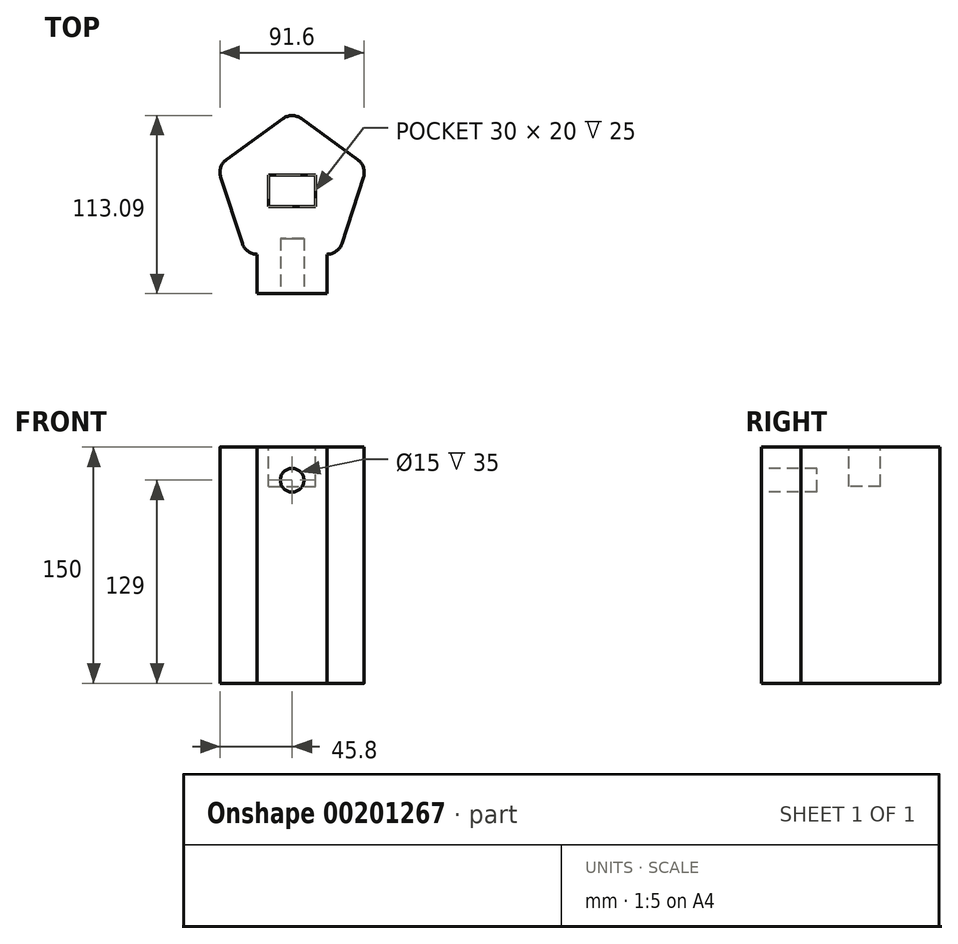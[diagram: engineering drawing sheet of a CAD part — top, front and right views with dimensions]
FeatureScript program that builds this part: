
annotation { "Feature Type Name" : "Feature", "Feature Type Description" : "" }
export const myFeature = defineFeature(function(context is Context, id is Id, definition is map)
    precondition{}
    {
        {
            var Q0;
            Q0=qCreatedBy(makeId("Top.planeOp"),FACE);
            var sketch = newSketch(context, id + "F0", { "sketchPlane" : qUnion([Q0])});
            skCircle(sketch, "E0.cCircle", {"center": v(0, 0) * mm, "radius": 50 * mm, "construction": true});
            skLineSegment(sketch, "E0.0", {"start": v(-47.55, 15.45) * mm, "end": v(0, 50) * mm});
            skLineSegment(sketch, "E0.1", {"start": v(0, 50) * mm, "end": v(47.55, 15.45) * mm});
            skLineSegment(sketch, "E0.2", {"start": v(47.55, 15.45) * mm, "end": v(29.39, -40.45) * mm});
            skLineSegment(sketch, "E0.3", {"start": v(29.39, -40.45) * mm, "end": v(-29.39, -40.45) * mm});
            skLineSegment(sketch, "E0.4", {"start": v(-29.39, -40.45) * mm, "end": v(-47.55, 15.45) * mm});
            skSolve(sketch);
        }
        {
            var Q0;
            Q0=makeQuery(id+"F0.imprint","IMPRINT",FACE,{"disambiguationData":[TD([[makeQuery(id+"F0.imprint","IMPRINT",EDGE,{"derivedFrom":sQuery(id+"F0.wireOp",EDGE,"E0.0")}),-1.0]])]});
            extrude(context, id + "F1", {"entities" : qUnion([Q0]), "depth" : 150 * mm});
        }
        {
            var Q0;
            Q0=makeQuery(id+"F1.opExtrude","SWEPT_EDGE",EDGE,{"disambiguationData":[OSD([sQuery(id+"F0.wireOp",EDGE,"E0.3"),sQuery(id+"F0.wireOp",EDGE,"E0.4")])]});
            var Q1;
            Q1=makeQuery(id+"F1.opExtrude","SWEPT_EDGE",EDGE,{"disambiguationData":[OSD([sQuery(id+"F0.wireOp",EDGE,"E0.0"),sQuery(id+"F0.wireOp",EDGE,"E0.4")])]});
            var Q2;
            Q2=makeQuery(id+"F1.opExtrude","SWEPT_EDGE",EDGE,{"disambiguationData":[OSD([sQuery(id+"F0.wireOp",EDGE,"E0.0"),sQuery(id+"F0.wireOp",EDGE,"E0.1")])]});
            var Q3;
            Q3=makeQuery(id+"F1.opExtrude","SWEPT_EDGE",EDGE,{"disambiguationData":[OSD([sQuery(id+"F0.wireOp",EDGE,"E0.1"),sQuery(id+"F0.wireOp",EDGE,"E0.2")])]});
            var Q4;
            Q4=makeQuery(id+"F1.opExtrude","SWEPT_EDGE",EDGE,{"disambiguationData":[OSD([sQuery(id+"F0.wireOp",EDGE,"E0.2"),sQuery(id+"F0.wireOp",EDGE,"E0.3")])]});
            fillet(context, id + "F2", {"entities" : qUnion([Q0, Q1, Q2, Q3, Q4]), "radius" : 10 * mm, "tangentPropagation" : true, "allowEdgeOverflow" : false});
        }
        {
            var Q0;
            Q0=qCreatedBy(makeId("Top.planeOp"),FACE);
            var sketch = newSketch(context, id + "F3", { "sketchPlane" : qUnion([Q0])});
            skCircle(sketch, "E1", {"center": v(0, 0) * mm, "radius": 50 * mm});
            skSolve(sketch);
        }
        {
            var Q0;
            Q0=makeQuery(id+"F1.opExtrude","CAP_FACE",FACE,{"disambiguationData":[OSD([sQuery(id+"F0.wireOp",EDGE,"E0.0"),sQuery(id+"F0.wireOp",EDGE,"E0.1"),sQuery(id+"F0.wireOp",EDGE,"E0.2"),sQuery(id+"F0.wireOp",EDGE,"E0.3"),sQuery(id+"F0.wireOp",EDGE,"E0.4")])],"isStart":false});
            var sketch = newSketch(context, id + "F4", { "sketchPlane" : qUnion([Q0])});
            skLineSegment(sketch, "E2.bottom", {"start": v(-15, 10) * mm, "end": v(15, 10) * mm});
            skLineSegment(sketch, "E2.top", {"start": v(-15, -10) * mm, "end": v(15, -10) * mm});
            skLineSegment(sketch, "E2.left", {"start": v(-15, 10) * mm, "end": v(-15, -10) * mm});
            skLineSegment(sketch, "E2.right", {"start": v(15, 10) * mm, "end": v(15, -10) * mm});
            skPoint(sketch, "E2.middle", {"position": v(0, 0) * mm});
            skSolve(sketch);
        }
        {
            var Q0;
            Q0=makeQuery(id+"F4.imprint","IMPRINT",FACE,{"disambiguationData":[TD([[makeQuery(id+"F4.imprint","IMPRINT",EDGE,{"derivedFrom":sQuery(id+"F4.wireOp",EDGE,"E2.bottom")}),-1.0]])]});
            extrude(context, id + "F5", {"entities" : qUnion([Q0]), "operationType" : NewBodyOperationType.REMOVE, "oppositeDirection" : true, "depth" : 25 * mm});
        }
        {
            var Q0;
            Q0=makeQuery(id+"F1.opExtrude","SWEPT_FACE",FACE,{"disambiguationData":[OSD([sQuery(id+"F0.wireOp",EDGE,"E0.3")])]});
            var sketch = newSketch(context, id + "F6", { "sketchPlane" : qUnion([Q0])});
            skCircle(sketch, "E3", {"center": v(0, 129) * mm, "radius": 7.5 * mm});
            skSolve(sketch);
        }
        {
            var Q0;
            Q0=makeQuery(id+"F6.imprint","IMPRINT",FACE,{"disambiguationData":[TD([[makeQuery(id+"F6.imprint","IMPRINT",EDGE,{"derivedFrom":sQuery(id+"F6.wireOp",EDGE,"E3")}),1.0]])]});
            extrude(context, id + "F7", {"entities" : qUnion([Q0]), "operationType" : NewBodyOperationType.REMOVE, "oppositeDirection" : true, "depth" : 10 * mm});
        }
        {
            var Q0;
            Q0=makeQuery(id+"F1.opExtrude","SWEPT_FACE",FACE,{"disambiguationData":[OSD([sQuery(id+"F0.wireOp",EDGE,"E0.3")])]});
            extrude(context, id + "F8", {"entities" : qUnion([Q0]), "operationType" : NewBodyOperationType.ADD, "depth" : 25 * mm});
        }
    });
